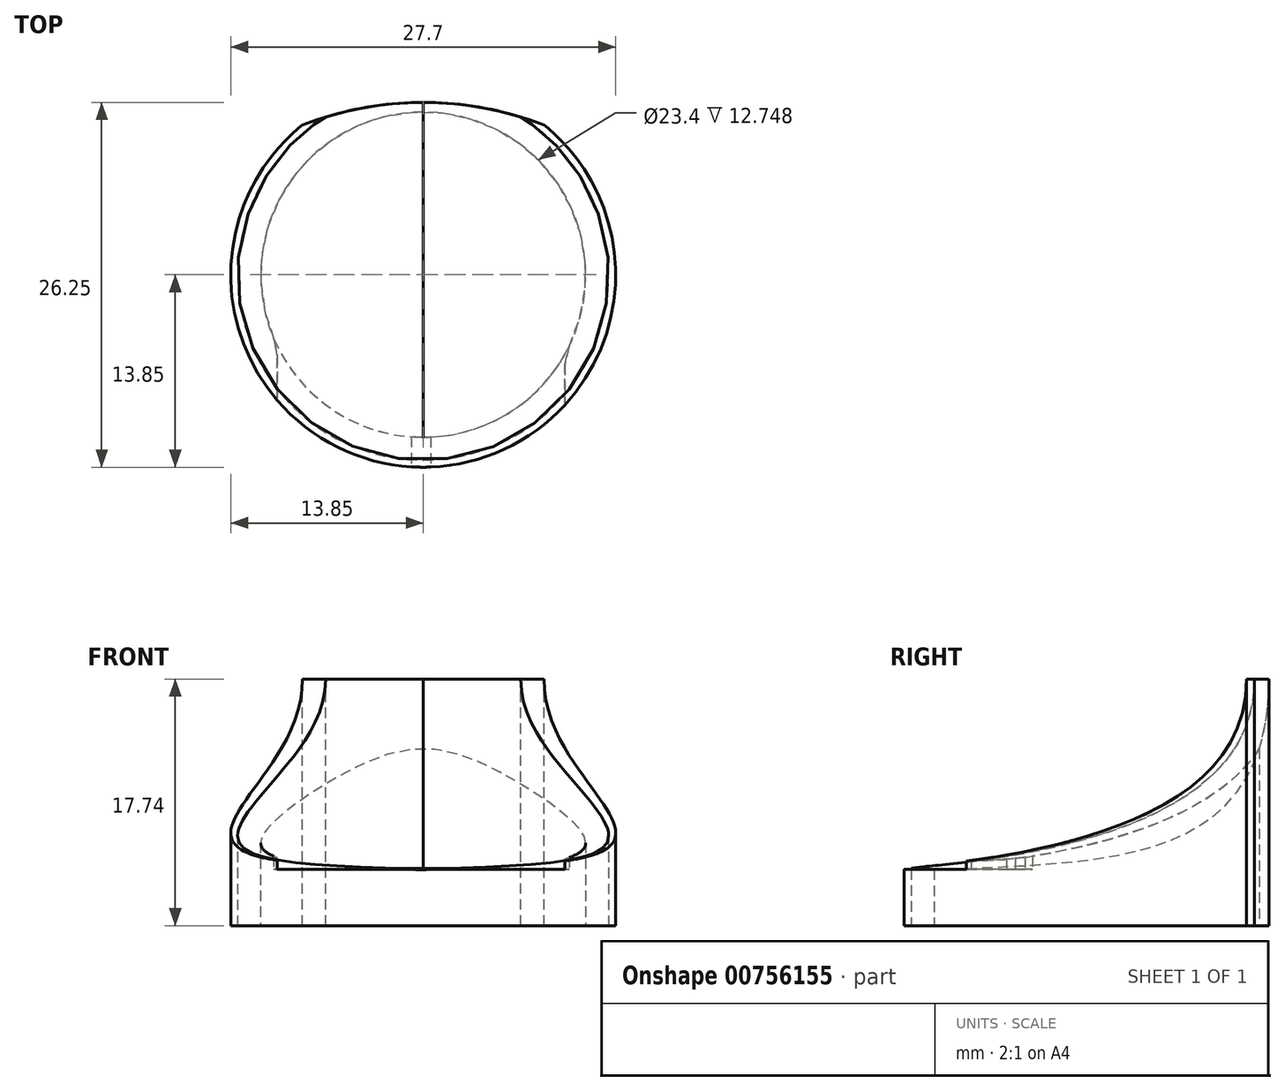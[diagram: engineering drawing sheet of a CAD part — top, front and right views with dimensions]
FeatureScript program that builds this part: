
annotation { "Feature Type Name" : "Feature", "Feature Type Description" : "" }
export const myFeature = defineFeature(function(context is Context, id is Id, definition is map)
    precondition{}
    {
        {
            var Q0;
            Q0=qCreatedBy(makeId("Top.planeOp"),FACE);
            var sketch = newSketch(context, id + "F0", { "sketchPlane" : qUnion([Q0])});
            skCircle(sketch, "E0", {"center": v(0, 0) * mm, "radius": 13.85 * mm});
            skCircle(sketch, "E1", {"center": v(0, 0) * mm, "radius": 11.7 * mm});
            skSolve(sketch);
        }
        {
            var Q0;
            Q0=makeQuery(id+"F0.imprint","IMPRINT",FACE,{"disambiguationData":[TD([[makeQuery(id+"F0.imprint","IMPRINT",EDGE,{"derivedFrom":sQuery(id+"F0.wireOp",EDGE,"E0")}),1.0]])]});
            extrude(context, id + "F1", {"entities" : qUnion([Q0]), "depth" : 35 * mm, "offsetDistance" : 25 * mm});
        }
        {
            var Q0;
            Q0=makeQuery(id+"F1.opExtrude","CAP_FACE",FACE,{"disambiguationData":[OSD([sQuery(id+"F0.wireOp",EDGE,"E0"),sQuery(id+"F0.wireOp",EDGE,"E1")])],"isStart":false});
            var sketch = newSketch(context, id + "F2", { "sketchPlane" : qUnion([Q0])});
            skCircle(sketch, "E2", {"center": v(0, 0) * mm, "radius": 11.3 * mm});
            skCircle(sketch, "E3.cCircle", {"center": v(0, 0) * mm, "radius": 11.7 * mm, "construction": true});
            skLineSegment(sketch, "E3.0", {"start": v(11.7, 0) * mm, "end": v(5.85, -10.13) * mm});
            skLineSegment(sketch, "E3.1", {"start": v(5.85, -10.13) * mm, "end": v(-5.85, -10.13) * mm});
            skLineSegment(sketch, "E3.2", {"start": v(-5.85, -10.13) * mm, "end": v(-11.7, 0) * mm});
            skLineSegment(sketch, "E3.3", {"start": v(-11.7, 0) * mm, "end": v(-5.85, 10.13) * mm});
            skLineSegment(sketch, "E3.4", {"start": v(-5.85, 10.13) * mm, "end": v(5.85, 10.13) * mm});
            skLineSegment(sketch, "E3.5", {"start": v(5.85, 10.13) * mm, "end": v(11.7, 0) * mm});
            skCircle(sketch, "E4", {"center": v(0, 0) * mm, "radius": 9.43 * mm});
            skSolve(sketch);
        }
        {
            var Q0;
            Q0=qSketchRegion(id+"F2",true);
            extrude(context, id + "F3", {"entities" : qUnion([Q0]), "depth" : 6 * mm, "offsetDistance" : 25 * mm});
        }
        {
            var Q0;
            Q0=makeQuery(id+"F1.opExtrude","CAP_FACE",FACE,{"disambiguationData":[OSD([sQuery(id+"F0.wireOp",EDGE,"E0"),sQuery(id+"F0.wireOp",EDGE,"E1")])],"isStart":false});
            var sketch = newSketch(context, id + "F4", { "sketchPlane" : qUnion([Q0])});
            skCircle(sketch, "E5", {"center": v(0, 0) * mm, "radius": 12.4 * mm});
            skCircle(sketch, "E6", {"center": v(0, 0) * mm, "radius": 10.27 * mm});
            skSolve(sketch);
        }
        {
            var Q0;
            Q0=qSketchRegion(id+"F4",true);
            extrude(context, id + "F5", {"entities" : qUnion([Q0]), "oppositeDirection" : true, "depth" : 4 * mm, "offsetDistance" : 25 * mm});
        }
        {
            var Q0;
            Q0=makeQuery(id+"F5.opExtrude","CAP_EDGE",EDGE,{"disambiguationData":[OSD([sQuery(id+"F4.wireOp",EDGE,"E6")])],"isStart":false});
            chamfer(context, id + "F6", {"entities" : qUnion([Q0]), "width" : 1 * mm, "tangentPropagation" : true});
        }
        {
            var Q0;
            Q0=makeQuery(id+"F3.opExtrude","CAP_EDGE",EDGE,{"disambiguationData":[OSD([sQuery(id+"F2.wireOp",EDGE,"E4")])],"isStart":false});
            fillet(context, id + "F7", {"entities" : qUnion([Q0]), "radius" : 1 * mm, "tangentPropagation" : true, "allowEdgeOverflow" : false});
        }
        {
            var Q0;
            Q0=makeQuery(id+"F1.opExtrude","CAP_FACE",FACE,{"disambiguationData":[OSD([sQuery(id+"F0.wireOp",EDGE,"E0"),sQuery(id+"F0.wireOp",EDGE,"E1")])],"isStart":true});
            var sketch = newSketch(context, id + "F8", { "sketchPlane" : qUnion([Q0])});
            skCircle(sketch, "E7", {"center": v(0, 0) * mm, "radius": 12.25 * mm});
            skSolve(sketch);
        }
        {
            var Q0;
            Q0=qSketchRegion(id+"F8",true);
            extrude(context, id + "F9", {"entities" : qUnion([Q0]), "operationType" : NewBodyOperationType.REMOVE, "oppositeDirection" : true, "depth" : 7 * mm, "offsetDistance" : 25 * mm});
        }
        {
            var Q0;
            Q0=qCreatedBy(makeId("Front.planeOp"),FACE);
            cPlane(context, id + "F10", {"entities" : qUnion([Q0]), "cplaneType" : CPlaneType.OFFSET, "offset" : 14 * mm, "width" : 150 * mm, "height" : 150 * mm});
        }
        {
            var Q0;
            Q0=qCreatedBy(id+"F10.planeOp",FACE);
            var sketch = newSketch(context, id + "F11", { "sketchPlane" : qUnion([Q0])});
            skLineSegment(sketch, "E8.bottom", {"start": v(-10.5, 35) * mm, "end": v(10.19, 35) * mm});
            skLineSegment(sketch, "E8.top", {"start": v(-0.87, 17.31) * mm, "end": v(0.55, 17.31) * mm});
            skLineSegment(sketch, "E8.left", {"start": v(-10.5, 35) * mm, "end": v(-10.5, 26.16) * mm});
            skLineSegment(sketch, "E8.right", {"start": v(10.19, 35) * mm, "end": v(10.19, 26.16) * mm});
            skArc(sketch, "E9", {"start": v(-0.87, 17.31) * mm, "mid": v(-0.16, 17.29) * mm, "end": v(0.55, 17.31) * mm});
            skPoint(sketch, "E10.orphan", {"position": v(-10.5, 17.31) * mm});
            skPoint(sketch, "E11.orphan", {"position": v(10.19, 17.31) * mm});
            skLineSegment(sketch, "E12.top", {"start": v(-10.5, 17.31) * mm, "end": v(10.19, 17.31) * mm});
            skLineSegment(sketch, "E12.left", {"start": v(-10.5, 26.16) * mm, "end": v(-10.5, 17.31) * mm});
            skLineSegment(sketch, "E12.right", {"start": v(10.19, 26.16) * mm, "end": v(10.19, 17.31) * mm});
            skSolve(sketch);
        }
        {
            var Q0;
            Q0 = qSketchRegion(id + "F11", true);
            extrude(context, id + "F12", {"entities" : qUnion([Q0]), "operationType" : NewBodyOperationType.REMOVE, "oppositeDirection" : true, "depth" : 13 * mm, "offsetDistance" : 25 * mm});
        }
        {
            var Q0;
            Q0=qCreatedBy(makeId("Top.planeOp"),FACE);
            var sketch = newSketch(context, id + "F13", { "sketchPlane" : qUnion([Q0])});
            skCircle(sketch, "E13", {"center": v(0, 0) * mm, "radius": 13.35 * mm});
            skSolve(sketch);
        }
        {
            var Q0;
            Q0 = qSketchRegion(id + "F13", true);
            extrude(context, id + "F14", {"entities" : qUnion([Q0]), "depth" : 34 * mm, "offsetDistance" : 25 * mm});
        }
        {
            var Q0;
            Q0=qCreatedBy(makeId("Right.planeOp"),FACE);
            var sketch = newSketch(context, id + "F15", { "sketchPlane" : qUnion([Q0])});
            skLineSegment(sketch, "E14", {"start": v(-11.7, 13.26) * mm, "end": v(12.4, 13.26) * mm});
            skLineSegment(sketch, "E15", {"start": v(12.4, 13.26) * mm, "end": v(12.4, 31) * mm});
            skLineSegment(sketch, "E16", {"start": v(-11.7, 17.29) * mm, "end": v(-11.7, 13.26) * mm});
            skFitSpline(sketch, "E17", {"points": [v(-11.7, 17.29) * mm, v(12.4, 31) * mm], "startDerivative": vector(35.1, 1.67) * mm, "endDerivative": vector(0, 41.3) * mm});
            skPoint(sketch, "E18", {"position": v(5.4, 16.28) * mm});
            skLineSegment(sketch, "E19", {"start": v(0, 50.16) * mm, "end": v(0, -20.76) * mm, "construction": true});
            skSolve(sketch);
        }
        {
            var Q0;
            Q0 = qSketchRegion(id + "F15", true);
            var Q1;
            Q1=sQuery(id+"F15.wireOp",EDGE,"E16");
            revolve(context, id + "F16", {"operationType" : NewBodyOperationType.INTERSECT, "surfaceOperationType" : NewSurfaceOperationType.NEW, "entities" : qUnion([Q0]), "axis" : qUnion([Q1]), "revolveType" : RevolveType.FULL});
        }
        {
            var Q0;
            Q0=makeQuery(id+"F12.boolean.opBoolean","INTERSECT",EDGE,{"derivedFrom":[makeQuery(id+"F1.opExtrude","SWEPT_FACE",FACE,{"disambiguationData":[OSD([sQuery(id+"F0.wireOp",EDGE,"E1")])]}),makeQuery(id+"F12.opExtrude","SWEPT_FACE",FACE,{"disambiguationData":[OSD([sQuery(id+"F11.wireOp",EDGE,"E8.right"),sQuery(id+"F11.wireOp",EDGE,"E12.right")])]})]});
            var Q1;
            Q1=makeQuery(id+"F12.boolean.opBoolean","INTERSECT",EDGE,{"derivedFrom":[makeQuery(id+"F1.opExtrude","SWEPT_FACE",FACE,{"disambiguationData":[OSD([sQuery(id+"F0.wireOp",EDGE,"E1")])]}),makeQuery(id+"F12.opExtrude","SWEPT_FACE",FACE,{"disambiguationData":[OSD([sQuery(id+"F11.wireOp",EDGE,"E8.left"),sQuery(id+"F11.wireOp",EDGE,"E12.left")])]})]});
            chamfer(context, id + "F17", {"entities" : qUnion([Q0, Q1]), "width" : 3 * mm, "tangentPropagation" : true});
        }
        {
            var Q0;
            Q0=qCreatedBy(id+"F10.planeOp",FACE);
            var sketch = newSketch(context, id + "F18", { "sketchPlane" : qUnion([Q0])});
            skLineSegment(sketch, "E20.bottom", {"start": v(-9.83, 45.73) * mm, "end": v(9.68, 45.73) * mm});
            skLineSegment(sketch, "E20.top", {"start": v(-9.83, 31.84) * mm, "end": v(9.68, 31.84) * mm});
            skLineSegment(sketch, "E20.left", {"start": v(-9.83, 45.73) * mm, "end": v(-9.83, 31.84) * mm});
            skLineSegment(sketch, "E20.right", {"start": v(9.68, 45.73) * mm, "end": v(9.68, 31.84) * mm});
            skSolve(sketch);
        }
        {
            var Q0;
            Q0 = qSketchRegion(id + "F18", true);
            extrude(context, id + "F19", {"entities" : qUnion([Q0]), "operationType" : NewBodyOperationType.REMOVE, "oppositeDirection" : true, "depth" : 10 * mm, "offsetDistance" : 25 * mm});
        }
    });
